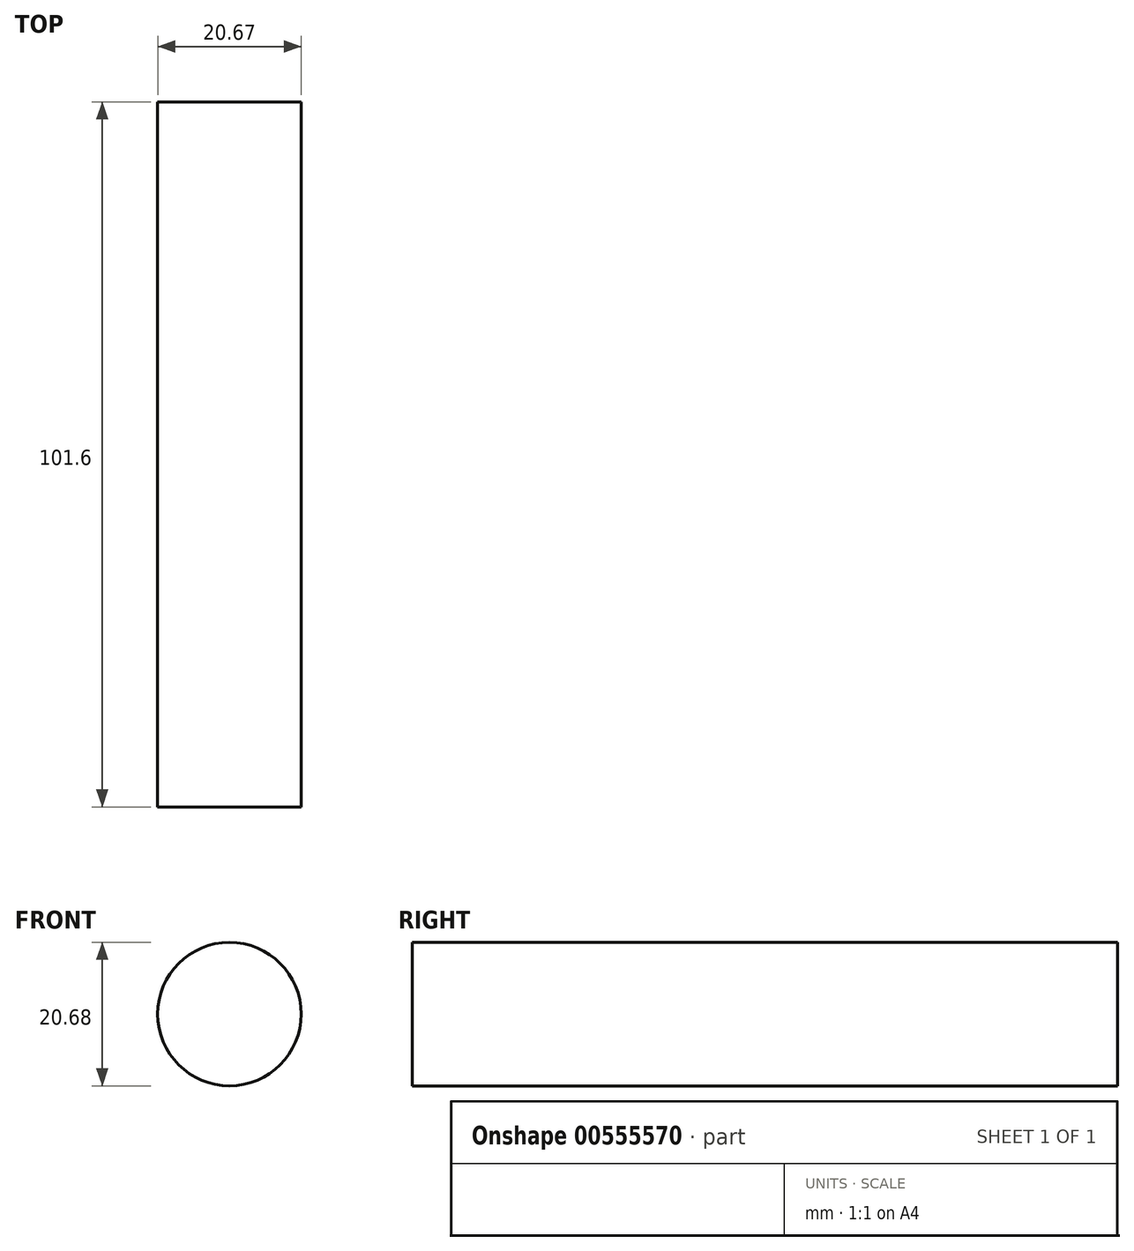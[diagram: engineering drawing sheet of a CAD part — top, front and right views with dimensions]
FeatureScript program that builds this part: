
annotation { "Feature Type Name" : "Feature", "Feature Type Description" : "" }
export const myFeature = defineFeature(function(context is Context, id is Id, definition is map)
    precondition{}
    {
        {
            var Q0;
            Q0=qCreatedBy(makeId("Front.planeOp"),FACE);
            var sketch = newSketch(context, id + "F0", { "sketchPlane" : qUnion([Q0])});
            skCircle(sketch, "E0", {"center": v(-30.19, 44.45) * mm, "radius": 10.34 * mm});
            skSolve(sketch);
        }
        {
            var Q0;
            Q0 = qSketchRegion(id + "F0", true);
            extrude(context, id + "F1", {"entities" : qUnion([Q0]), "depth" : 101.6 * mm, "offsetDistance" : 25.4 * mm});
        }
    });
